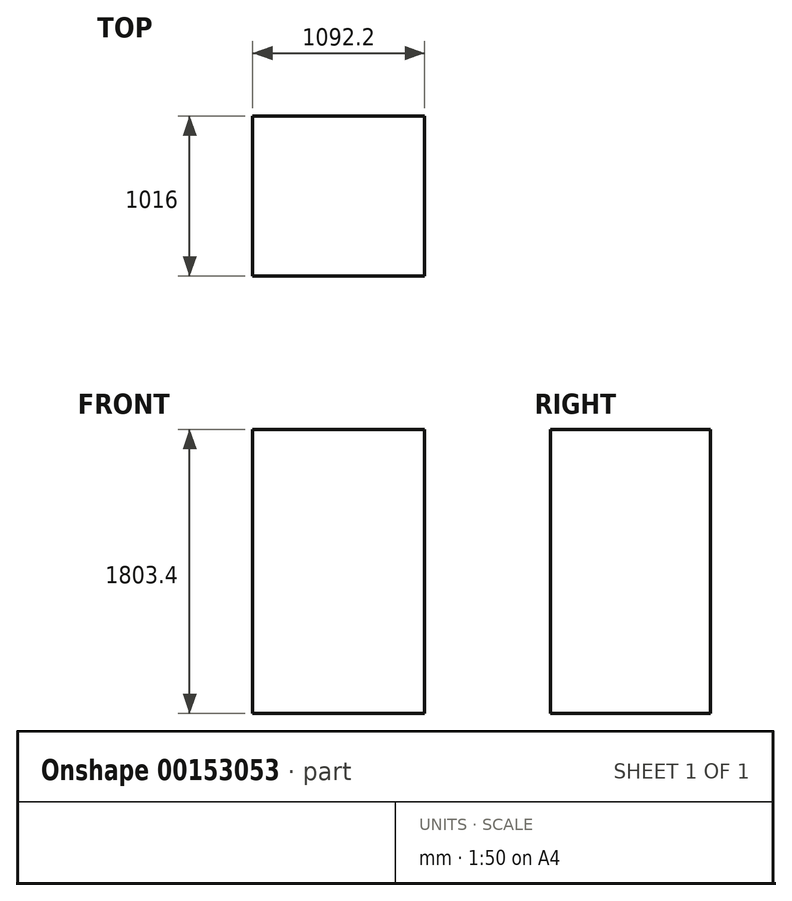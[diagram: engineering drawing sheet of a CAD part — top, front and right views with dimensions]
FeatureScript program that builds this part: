
annotation { "Feature Type Name" : "Feature", "Feature Type Description" : "" }
export const myFeature = defineFeature(function(context is Context, id is Id, definition is map)
    precondition{}
    {
        {
            var Q0;
            Q0=qCreatedBy(makeId("Top.planeOp"),FACE);
            var sketch = newSketch(context, id + "F0", { "sketchPlane" : qUnion([Q0])});
            skLineSegment(sketch, "E0.bottom", {"start": v(0, 0) * mm, "end": v(-1092.2, 0) * mm});
            skLineSegment(sketch, "E0.top", {"start": v(0, -1016) * mm, "end": v(-1092.2, -1016) * mm});
            skLineSegment(sketch, "E0.left", {"start": v(0, 0) * mm, "end": v(0, -1016) * mm});
            skLineSegment(sketch, "E0.right", {"start": v(-1092.2, 0) * mm, "end": v(-1092.2, -1016) * mm});
            skSolve(sketch);
        }
        {
            var Q0;
            Q0 = qSketchRegion(id + "F0", true);
            extrude(context, id + "F1", {"entities" : qUnion([Q0]), "depth" : 1803.4 * mm});
        }
    });
